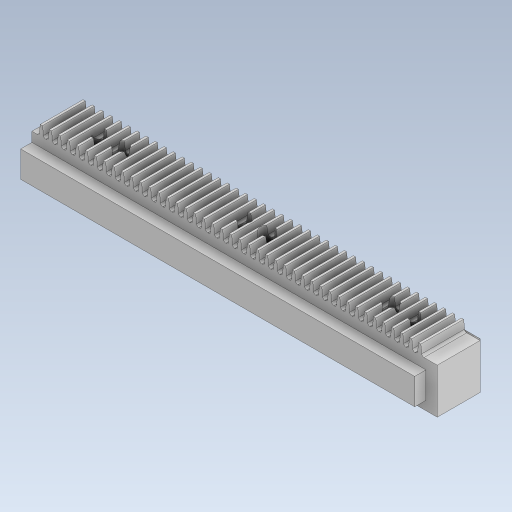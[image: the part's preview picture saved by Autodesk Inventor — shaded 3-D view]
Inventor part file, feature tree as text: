
AUTODESK INVENTOR PART (.ipt)
format: ipt  version: 2023.5 (Build 275446000, 446)  size: 1,275,904 bytes
history: native  units: in
note: dims shown in document units (in); Inventor stores cm internally (conversion verified against a paired STEP export)
features: extrude x9, sketch x8, plane x2, fillet x1, pattern_linear x1
ambient origin geometry x8: Origin, YZ Plane, XZ Plane, XY Plane, X Axis, Y Axis, Z Axis, Center Point
bodies: Solid1 (feature_tree)
feature tree (21):
  sketch  "Sketch1"  dims[d0=3.937in d1=0.748in]
  extrude  "Extrusion1"  Depth=0.748in
  extrude  "Extrusion2"  Depth=0.1969in
  extrude  "Extrusion3"  Depth=0.1969in
  plane  "Work Plane1"
  extrude  "Extrusion5"  Depth=0.4606in
  fillet  "Fillet1"  Radius=0.1969in
  extrude  "Extrusion7"  Depth=0.1969in TaperAngle=0.0deg
  extrude  "Extrusion9"  Depth=0.0394in
  pattern_linear  "Rectangular Pattern2"  Spacing1=0.0394in  [1 undecoded]
  extrude  "Extrusion10"  Depth=0.1181in TaperAngle=0.0deg
  plane  "Work Plane3"
  extrude  "Extrusion11"  Depth=0.1181in TaperAngle=0.0deg
  extrude  "Extrusion12"  Depth=0.1181in
  sketch  "Sketch3"  dims[d2=0.1969in d3=0.1969in]
  sketch  "Sketch4"  dims[d4=0.1969in d5=0.1969in]
  sketch  "Sketch7"  dims[d6=0.7874in d7=0.0in d8=0.4606in d9=0.1969in d10=0.0in]
  sketch  "Sketch10"  dims[d11=0.4606in d12=0.1969in d13=0.0in]
  sketch  "Sketch11"  dims[d27=3.7402in d28=0.0394in]
  sketch  "Sketch12"  dims[d29=0.0748in]
  sketch  "Sketch13"  dims[d30=0.374in d31=0.374in d32=0.0in d33=0.0in d34=0.0394in d45=0.7874in d46=0.0in d55=3.1496in d56=0.0in d57=16.9291in d59=0.1575in d60=0.1181in d61=0.7874in d62=0.1181in d63=0.3937in d64=0.1181in d65=0.7874in d66=0.1181in d67=0.3937in d68=0.1181in d69=0.1969in d70=1.1811in d71=0.0in d72=0.2362in d73=0.2362in d74=0.2362in d75=0.2362in d76=0.2362in d77=0.1969in d78=0.5906in d79=0.0in d80=0.1969in d81=0.0in]
note: 1 required parameter value undecoded (feature->parameter linkage not recoverable at this tier; creation-order binding heuristic only, values carry confidence <= 0.55)
